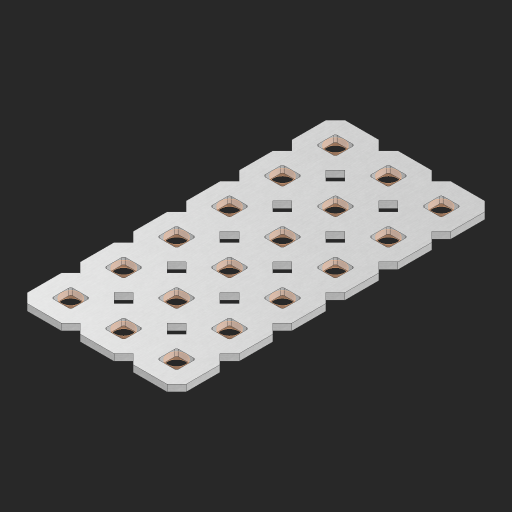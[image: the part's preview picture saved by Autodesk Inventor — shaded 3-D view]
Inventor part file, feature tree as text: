
AUTODESK INVENTOR PART (.ipt)
format: ipt  version: 2023 (Build 270158000, 158)  size: 504,320 bytes
history: native  units: in
note: dims shown in document units (in); Inventor stores cm internally (conversion verified against a paired STEP export)
features: other x19, extrude x17, sketch x2, pattern_linear x1
ambient origin geometry x8: Origin, YZ Plane, XZ Plane, XY Plane, X Axis, Y Axis, Z Axis, Center Point
bodies: Solid1 (feature_tree), Body (feature_tree)
feature tree (39):
  pattern_linear  "Rectangular Pattern1"  Spacing1=0.09in  [1 undecoded]
  sketch  "Sketch1"  dims[d1=0.5in]
  sketch  "Sketch2"  dims[d2=0.182in d3=0.09in d4=0.09in d5=0.09in d6=0.09in d7=0.09in d8=0.09in d9=0.09in d10=0.09in d11=0.02in d13=0.0in d14=0.172in d15=0.0625in d16=0.0in d19=0.5in d22=0.5in]
  other  "Srf1"
  other  "Srf126"
  other  "Srf127"
  other  "Srf128"
  other  "Srf129"
  other  "Srf130"
  other  "Srf268"
  other  "Srf269"
  other  "Srf270"
  other  "Srf271"
  other  "Srf272"
  other  "Srf273"
  other  "Srf293"
  other  "Srf294"
  other  "Srf295"
  other  "Srf296"
  other  "Srf297"
  other  "Srf298"
  other  "Circle"
  extrude  "ExtrusionSrf126"  Depth=0.09in
  extrude  "ExtrusionSrf127"  Depth=0.09in
  extrude  "ExtrusionSrf128"  Depth=0.09in
  extrude  "ExtrusionSrf129"  Depth=0.09in
  extrude  "ExtrusionSrf130"  Depth=0.09in
  extrude  "ExtrusionSrf268"  Depth=0.09in
  extrude  "ExtrusionSrf269"  Depth=0.09in
  extrude  "ExtrusionSrf270"  Depth=0.02in
  extrude  "ExtrusionSrf271"  TaperAngle=0.0deg  [1 undecoded]
  extrude  "ExtrusionSrf272"  Depth=0.5in
  extrude  "ExtrusionSrf273"  Depth=0.0625in TaperAngle=0.0deg
  extrude  "ExtrusionSrf293"  Depth=0.5in
  extrude  "ExtrusionSrf294"  Depth=0.5in
  extrude  "ExtrusionSrf295"  [1 undecoded]
  extrude  "ExtrusionSrf296"  [1 undecoded]
  extrude  "ExtrusionSrf297"  [1 undecoded]
  extrude  "ExtrusionSrf298"  [1 undecoded]
note: 6 required parameter values undecoded (feature->parameter linkage not recoverable at this tier; creation-order binding heuristic only, values carry confidence <= 0.55)
